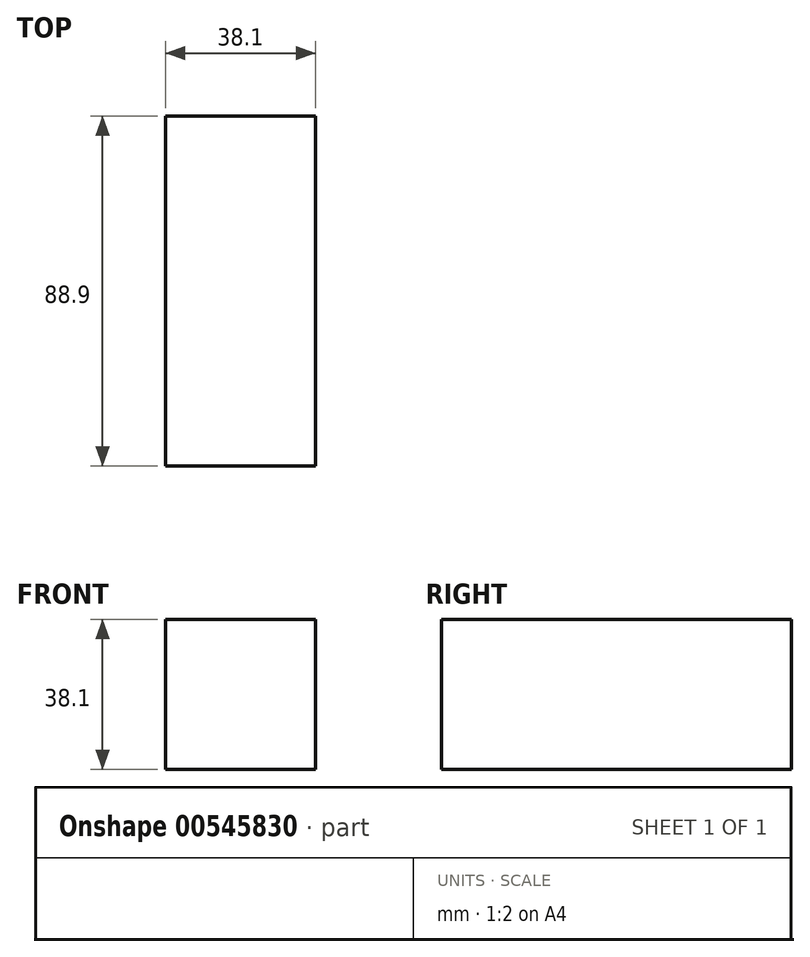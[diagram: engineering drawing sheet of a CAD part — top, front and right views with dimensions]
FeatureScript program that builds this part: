
annotation { "Feature Type Name" : "Feature", "Feature Type Description" : "" }
export const myFeature = defineFeature(function(context is Context, id is Id, definition is map)
    precondition{}
    {
        {
            var Q0;
            Q0=qCreatedBy(makeId("Top.planeOp"),FACE);
            var sketch = newSketch(context, id + "F0", { "sketchPlane" : qUnion([Q0])});
            skLineSegment(sketch, "E0.bottom", {"start": v(19.05, 44.45) * mm, "end": v(-19.05, 44.45) * mm});
            skLineSegment(sketch, "E0.top", {"start": v(19.05, -44.45) * mm, "end": v(-19.05, -44.45) * mm});
            skLineSegment(sketch, "E0.left", {"start": v(19.05, 44.45) * mm, "end": v(19.05, -44.45) * mm});
            skLineSegment(sketch, "E0.right", {"start": v(-19.05, 44.45) * mm, "end": v(-19.05, -44.45) * mm});
            skPoint(sketch, "E0.middle", {"position": v(0, 0) * mm});
            skSolve(sketch);
        }
        {
            var Q0;
            Q0=makeQuery(id+"F0.imprint","IMPRINT",FACE,{"disambiguationData":[TD([[makeQuery(id+"F0.imprint","IMPRINT",EDGE,{"derivedFrom":sQuery(id+"F0.wireOp",EDGE,"E0.bottom")}),1.0]])]});
            extrude(context, id + "F1", {"entities" : qUnion([Q0]), "depth" : 38.1 * mm, "offsetDistance" : 25.4 * mm, "symmetric" : true});
        }
    });
